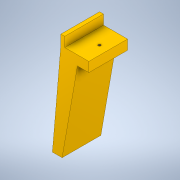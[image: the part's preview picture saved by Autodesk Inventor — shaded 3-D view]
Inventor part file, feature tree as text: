
AUTODESK INVENTOR PART (.ipt)
format: ipt  version: 2022 (Build 260153000, 153)  size: 157,184 bytes
history: native  units: in
note: dims shown in document units (in); Inventor stores cm internally (conversion verified against a paired STEP export)
features: extrude x4, sketch x4, thread x1
ambient origin geometry x8: Origin, YZ Plane, XZ Plane, XY Plane, X Axis, Y Axis, Z Axis, Center Point
bodies: Solid1 (feature_tree)
feature tree (9):
  extrude  "Extrusion1"  Depth=0.25in
  extrude  "Extrusion2"  Depth=0.25in
  extrude  "Extrusion3"  Depth=5.0in
  extrude  "Extrusion4"  Depth=0.5in TaperAngle=0.0deg
  thread  "Thread1"  [1 undecoded]
  sketch  "Sketch1"  dims[d0=0.25in d2=0.5841in]
  sketch  "Sketch2"  dims[d3=0.25in d6=0.5497in]
  sketch  "Sketch4"  dims[d7=2.0in d8=0.0in d9=5.0in]
  sketch  "Sketch5"  dims[d10=0.2in d11=0.5in d12=0.0in d14=0.5in d15=0.5in d16=0.0in d18=0.138in d19=0.45in d20=1.0in d21=0.5in d22=0.0in d23=0.5in d24=0.0in d25=0.0in d26=0.0in d27=0.0in d28=0.0in]
note: 1 required parameter value undecoded (feature->parameter linkage not recoverable at this tier; creation-order binding heuristic only, values carry confidence <= 0.55)
